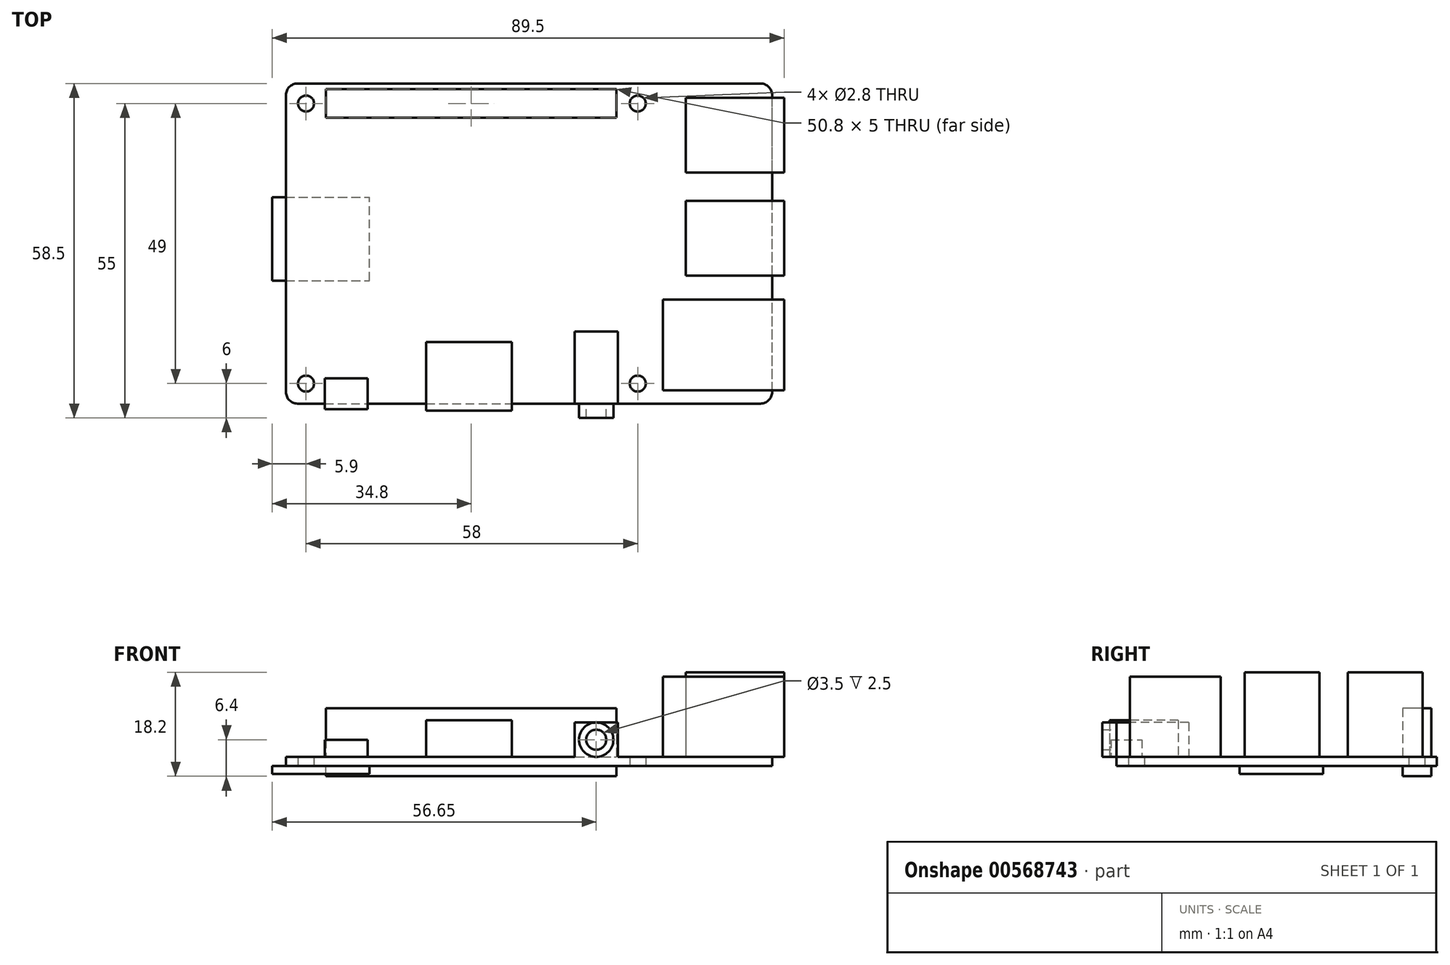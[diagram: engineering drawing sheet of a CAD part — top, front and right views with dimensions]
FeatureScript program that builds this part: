
annotation { "Feature Type Name" : "Feature", "Feature Type Description" : "" }
export const myFeature = defineFeature(function(context is Context, id is Id, definition is map)
    precondition{}
    {
        {
            var Q0;
            Q0=qCreatedBy(makeId("Top.planeOp"),FACE);
            var sketch = newSketch(context, id + "F0", { "sketchPlane" : qUnion([Q0])});
            skLineSegment(sketch, "E0.bottom", {"start": v(2, 0) * mm, "end": v(83, 0) * mm});
            skLineSegment(sketch, "E0.top", {"start": v(2, 56) * mm, "end": v(83, 56) * mm});
            skLineSegment(sketch, "E0.left", {"start": v(0, 2) * mm, "end": v(0, 54) * mm});
            skLineSegment(sketch, "E0.right", {"start": v(85, 2) * mm, "end": v(85, 54) * mm});
            skPoint(sketch, "E1.visualSharp", {"position": v(0, 56) * mm});
            skArc(sketch, "E1.filletArc", {"start": v(2, 56) * mm, "mid": v(0.59, 55.41) * mm, "end": v(0, 54) * mm});
            skPoint(sketch, "E2.visualSharp", {"position": v(85, 56) * mm});
            skArc(sketch, "E2.filletArc", {"start": v(85, 54) * mm, "mid": v(84.41, 55.41) * mm, "end": v(83, 56) * mm});
            skPoint(sketch, "E3.visualSharp", {"position": v(85, 0) * mm});
            skArc(sketch, "E3.filletArc", {"start": v(83, 0) * mm, "mid": v(84.41, 0.59) * mm, "end": v(85, 2) * mm});
            skPoint(sketch, "E4.visualSharp", {"position": v(0, 0) * mm});
            skArc(sketch, "E4.filletArc", {"start": v(0, 2) * mm, "mid": v(0.59, 0.59) * mm, "end": v(2, 0) * mm});
            skCircle(sketch, "E5", {"center": v(3.5, 52.5) * mm, "radius": 1.4 * mm});
            skCircle(sketch, "E6", {"center": v(61.5, 52.5) * mm, "radius": 1.4 * mm});
            skCircle(sketch, "E7", {"center": v(61.5, 3.5) * mm, "radius": 1.4 * mm});
            skCircle(sketch, "E8", {"center": v(3.5, 3.5) * mm, "radius": 1.4 * mm});
            skSolve(sketch);
        }
        {
            var Q0;
            Q0=makeQuery(id+"F0.imprint","IMPRINT",FACE,{"disambiguationData":[TD([[makeQuery(id+"F0.imprint","IMPRINT",EDGE,{"derivedFrom":sQuery(id+"F0.wireOp",EDGE,"E0.bottom")}),1.0]])]});
            extrude(context, id + "F1", {"entities" : qUnion([Q0]), "depth" : 1.6 * mm, "offsetDistance" : 25 * mm});
        }
        {
            var Q0;
            Q0=makeQuery(id+"F1.opExtrude","CAP_FACE",FACE,{"disambiguationData":[OSD([sQuery(id+"F0.wireOp",EDGE,"E0.bottom"),sQuery(id+"F0.wireOp",EDGE,"E0.top"),sQuery(id+"F0.wireOp",EDGE,"E0.left"),sQuery(id+"F0.wireOp",EDGE,"E0.right"),sQuery(id+"F0.wireOp",EDGE,"E1.filletArc"),sQuery(id+"F0.wireOp",EDGE,"E2.filletArc"),sQuery(id+"F0.wireOp",EDGE,"E3.filletArc"),sQuery(id+"F0.wireOp",EDGE,"E4.filletArc"),sQuery(id+"F0.wireOp",EDGE,"E5"),sQuery(id+"F0.wireOp",EDGE,"E6"),sQuery(id+"F0.wireOp",EDGE,"E7"),sQuery(id+"F0.wireOp",EDGE,"E8")])],"isStart":false});
            var sketch = newSketch(context, id + "F2", { "sketchPlane" : qUnion([Q0])});
            skLineSegment(sketch, "E9.bottom", {"start": v(87.1, 53.5) * mm, "end": v(69.9, 53.5) * mm});
            skLineSegment(sketch, "E9.top", {"start": v(87.1, 40.4) * mm, "end": v(69.9, 40.4) * mm});
            skLineSegment(sketch, "E9.left", {"start": v(87.1, 53.5) * mm, "end": v(87.1, 40.4) * mm});
            skLineSegment(sketch, "E9.right", {"start": v(69.9, 53.5) * mm, "end": v(69.9, 40.4) * mm});
            skLineSegment(sketch, "E10.bottom", {"start": v(87.1, 35.5) * mm, "end": v(69.9, 35.5) * mm});
            skLineSegment(sketch, "E10.top", {"start": v(87.1, 22.4) * mm, "end": v(69.9, 22.4) * mm});
            skLineSegment(sketch, "E10.left", {"start": v(87.1, 35.5) * mm, "end": v(87.1, 22.4) * mm});
            skLineSegment(sketch, "E10.right", {"start": v(69.9, 35.5) * mm, "end": v(69.9, 22.4) * mm});
            skLineSegment(sketch, "E11.bottom", {"start": v(87.1, 18.2) * mm, "end": v(65.9, 18.2) * mm});
            skLineSegment(sketch, "E11.top", {"start": v(87.1, 2.3) * mm, "end": v(65.9, 2.3) * mm});
            skLineSegment(sketch, "E11.left", {"start": v(87.1, 18.2) * mm, "end": v(87.1, 2.3) * mm});
            skLineSegment(sketch, "E11.right", {"start": v(65.9, 18.2) * mm, "end": v(65.9, 2.3) * mm});
            skSolve(sketch);
        }
        {
            var Q0;
            {var subQ0=sQuery(id+"F2.wireOp",EDGE,"E9.right");Q0=makeQuery(id+"F2.imprint","IMPRINT",FACE,{"disambiguationData":[TD([[makeQuery(id+"F2.imprint","IMPRINT",EDGE,{"derivedFrom":subQ0}),1.0]])]});}
            var Q1;
            {var subQ0=sQuery(id+"F2.wireOp",EDGE,"E9.left");Q1=makeQuery(id+"F2.imprint","IMPRINT",FACE,{"disambiguationData":[TD([[makeQuery(id+"F2.imprint","IMPRINT",EDGE,{"derivedFrom":subQ0}),-1.0]])]});}
            var Q2;
            {var subQ0=sQuery(id+"F2.wireOp",EDGE,"E10.right");Q2=makeQuery(id+"F2.imprint","IMPRINT",FACE,{"disambiguationData":[TD([[makeQuery(id+"F2.imprint","IMPRINT",EDGE,{"derivedFrom":subQ0}),1.0]])]});}
            var Q3;
            {var subQ0=sQuery(id+"F2.wireOp",EDGE,"E10.left");Q3=makeQuery(id+"F2.imprint","IMPRINT",FACE,{"disambiguationData":[TD([[makeQuery(id+"F2.imprint","IMPRINT",EDGE,{"derivedFrom":subQ0}),-1.0]])]});}
            extrude(context, id + "F3", {"entities" : qUnion([Q0, Q1, Q2, Q3]), "operationType" : NewBodyOperationType.ADD, "depth" : 14.8 * mm, "offsetDistance" : 25 * mm});
        }
        {
            var Q0;
            {var subQ0=sQuery(id+"F2.wireOp",EDGE,"E11.right");Q0=makeQuery(id+"F2.imprint","IMPRINT",FACE,{"disambiguationData":[TD([[makeQuery(id+"F2.imprint","IMPRINT",EDGE,{"derivedFrom":subQ0}),1.0]])]});}
            var Q1;
            {var subQ0=sQuery(id+"F2.wireOp",EDGE,"E11.left");Q1=makeQuery(id+"F2.imprint","IMPRINT",FACE,{"disambiguationData":[TD([[makeQuery(id+"F2.imprint","IMPRINT",EDGE,{"derivedFrom":subQ0}),-1.0]])]});}
            extrude(context, id + "F4", {"entities" : qUnion([Q0, Q1]), "operationType" : NewBodyOperationType.ADD, "depth" : 14 * mm, "offsetDistance" : 25 * mm});
        }
        {
            var Q0;
            Q0=makeQuery(id+"F1.opExtrude","CAP_FACE",FACE,{"disambiguationData":[OSD([sQuery(id+"F0.wireOp",EDGE,"E0.bottom"),sQuery(id+"F0.wireOp",EDGE,"E0.top"),sQuery(id+"F0.wireOp",EDGE,"E0.left"),sQuery(id+"F0.wireOp",EDGE,"E0.right"),sQuery(id+"F0.wireOp",EDGE,"E1.filletArc"),sQuery(id+"F0.wireOp",EDGE,"E2.filletArc"),sQuery(id+"F0.wireOp",EDGE,"E3.filletArc"),sQuery(id+"F0.wireOp",EDGE,"E4.filletArc"),sQuery(id+"F0.wireOp",EDGE,"E5"),sQuery(id+"F0.wireOp",EDGE,"E6"),sQuery(id+"F0.wireOp",EDGE,"E7"),sQuery(id+"F0.wireOp",EDGE,"E8")])],"isStart":false});
            var sketch = newSketch(context, id + "F5", { "sketchPlane" : qUnion([Q0])});
            skLineSegment(sketch, "E12.bottom", {"start": v(7, 55) * mm, "end": v(57.8, 55) * mm});
            skLineSegment(sketch, "E12.top", {"start": v(7, 50) * mm, "end": v(57.8, 50) * mm});
            skLineSegment(sketch, "E12.left", {"start": v(7, 55) * mm, "end": v(7, 50) * mm});
            skLineSegment(sketch, "E12.right", {"start": v(57.8, 55) * mm, "end": v(57.8, 50) * mm});
            skSolve(sketch);
        }
        {
            var Q0;
            Q0=makeQuery(id+"F5.imprint","IMPRINT",FACE,{"disambiguationData":[TD([[makeQuery(id+"F5.imprint","IMPRINT",EDGE,{"derivedFrom":sQuery(id+"F5.wireOp",EDGE,"E12.bottom")}),-1.0]])]});
            extrude(context, id + "F6", {"entities" : qUnion([Q0]), "operationType" : NewBodyOperationType.ADD, "depth" : 8.5 * mm, "offsetDistance" : 25 * mm});
        }
        {
            var Q0;
            Q0 = qSketchRegion(id + "F5", true);
            extrude(context, id + "F7", {"entities" : qUnion([Q0]), "operationType" : NewBodyOperationType.ADD, "oppositeDirection" : true, "depth" : (1.6 + 1.8) * mm, "offsetDistance" : 25 * mm});
        }
        {
            var Q0;
            Q0=makeQuery(id+"F1.opExtrude","CAP_FACE",FACE,{"disambiguationData":[OSD([sQuery(id+"F0.wireOp",EDGE,"E0.bottom"),sQuery(id+"F0.wireOp",EDGE,"E0.top"),sQuery(id+"F0.wireOp",EDGE,"E0.left"),sQuery(id+"F0.wireOp",EDGE,"E0.right"),sQuery(id+"F0.wireOp",EDGE,"E1.filletArc"),sQuery(id+"F0.wireOp",EDGE,"E2.filletArc"),sQuery(id+"F0.wireOp",EDGE,"E3.filletArc"),sQuery(id+"F0.wireOp",EDGE,"E4.filletArc"),sQuery(id+"F0.wireOp",EDGE,"E5"),sQuery(id+"F0.wireOp",EDGE,"E6"),sQuery(id+"F0.wireOp",EDGE,"E7"),sQuery(id+"F0.wireOp",EDGE,"E8")])],"isStart":true});
            var sketch = newSketch(context, id + "F8", { "sketchPlane" : qUnion([Q0])});
            skLineSegment(sketch, "E13.bottom", {"start": v(-2.4, -21.5) * mm, "end": v(14.6, -21.5) * mm});
            skLineSegment(sketch, "E13.top", {"start": v(-2.4, -36.1) * mm, "end": v(14.6, -36.1) * mm});
            skLineSegment(sketch, "E13.left", {"start": v(-2.4, -21.5) * mm, "end": v(-2.4, -36.1) * mm});
            skLineSegment(sketch, "E13.right", {"start": v(14.6, -21.5) * mm, "end": v(14.6, -36.1) * mm});
            skSolve(sketch);
        }
        {
            var Q0;
            Q0 = qSketchRegion(id + "F8", true);
            extrude(context, id + "F9", {"entities" : qUnion([Q0]), "operationType" : NewBodyOperationType.ADD, "depth" : 1.4 * mm, "offsetDistance" : 25 * mm});
        }
        {
            var Q0;
            Q0=makeQuery(id+"F1.opExtrude","CAP_FACE",FACE,{"disambiguationData":[OSD([sQuery(id+"F0.wireOp",EDGE,"E0.bottom"),sQuery(id+"F0.wireOp",EDGE,"E0.top"),sQuery(id+"F0.wireOp",EDGE,"E0.left"),sQuery(id+"F0.wireOp",EDGE,"E0.right"),sQuery(id+"F0.wireOp",EDGE,"E1.filletArc"),sQuery(id+"F0.wireOp",EDGE,"E2.filletArc"),sQuery(id+"F0.wireOp",EDGE,"E3.filletArc"),sQuery(id+"F0.wireOp",EDGE,"E4.filletArc"),sQuery(id+"F0.wireOp",EDGE,"E5"),sQuery(id+"F0.wireOp",EDGE,"E6"),sQuery(id+"F0.wireOp",EDGE,"E7"),sQuery(id+"F0.wireOp",EDGE,"E8")])],"isStart":false});
            var sketch = newSketch(context, id + "F10", { "sketchPlane" : qUnion([Q0])});
            skLineSegment(sketch, "E14.bottom", {"start": v(24.5, 10.8) * mm, "end": v(39.5, 10.8) * mm});
            skLineSegment(sketch, "E14.top", {"start": v(24.5, -1.2) * mm, "end": v(39.5, -1.2) * mm});
            skLineSegment(sketch, "E14.left", {"start": v(24.5, 10.8) * mm, "end": v(24.5, -1.2) * mm});
            skLineSegment(sketch, "E14.right", {"start": v(39.5, 10.8) * mm, "end": v(39.5, -1.2) * mm});
            skLineSegment(sketch, "E15.bottom", {"start": v(50.5, 12.6) * mm, "end": v(58, 12.6) * mm});
            skLineSegment(sketch, "E15.top", {"start": v(50.5, 0) * mm, "end": v(58, 0) * mm});
            skLineSegment(sketch, "E15.left", {"start": v(50.5, 12.6) * mm, "end": v(50.5, 0) * mm});
            skLineSegment(sketch, "E15.right", {"start": v(58, 12.6) * mm, "end": v(58, 0) * mm});
            skLineSegment(sketch, "E16.bottom", {"start": v(6.8, -1) * mm, "end": v(14.3, -1) * mm});
            skLineSegment(sketch, "E16.top", {"start": v(6.8, 4.4) * mm, "end": v(14.3, 4.4) * mm});
            skLineSegment(sketch, "E16.left", {"start": v(6.8, -1) * mm, "end": v(6.8, 4.4) * mm});
            skLineSegment(sketch, "E16.right", {"start": v(14.3, -1) * mm, "end": v(14.3, 4.4) * mm});
            skSolve(sketch);
        }
        {
            var Q0;
            {var subQ0=sQuery(id+"F10.wireOp",EDGE,"E16.top");Q0=makeQuery(id+"F10.imprint","IMPRINT",FACE,{"disambiguationData":[TD([[makeQuery(id+"F10.imprint","IMPRINT",EDGE,{"derivedFrom":subQ0}),-1.0]])]});}
            var Q1;
            {var subQ0=sQuery(id+"F10.wireOp",EDGE,"E16.bottom");Q1=makeQuery(id+"F10.imprint","IMPRINT",FACE,{"disambiguationData":[TD([[makeQuery(id+"F10.imprint","IMPRINT",EDGE,{"derivedFrom":subQ0}),1.0]])]});}
            extrude(context, id + "F11", {"entities" : qUnion([Q0, Q1]), "operationType" : NewBodyOperationType.ADD, "depth" : 3 * mm, "offsetDistance" : 25 * mm});
        }
        {
            var Q0;
            {var subQ0=sQuery(id+"F10.wireOp",EDGE,"E14.bottom");Q0=makeQuery(id+"F10.imprint","IMPRINT",FACE,{"disambiguationData":[TD([[makeQuery(id+"F10.imprint","IMPRINT",EDGE,{"derivedFrom":subQ0}),-1.0]])]});}
            var Q1;
            {var subQ0=sQuery(id+"F10.wireOp",EDGE,"E14.top");Q1=makeQuery(id+"F10.imprint","IMPRINT",FACE,{"disambiguationData":[TD([[makeQuery(id+"F10.imprint","IMPRINT",EDGE,{"derivedFrom":subQ0}),1.0]])]});}
            extrude(context, id + "F12", {"entities" : qUnion([Q0, Q1]), "operationType" : NewBodyOperationType.ADD, "depth" : 6.4 * mm, "offsetDistance" : 25 * mm});
        }
        {
            var Q0;
            Q0=makeQuery(id+"F10.imprint","IMPRINT",FACE,{"disambiguationData":[TD([[makeQuery(id+"F10.imprint","IMPRINT",EDGE,{"derivedFrom":sQuery(id+"F10.wireOp",EDGE,"E15.bottom")}),-1.0]])]});
            extrude(context, id + "F13", {"entities" : qUnion([Q0]), "operationType" : NewBodyOperationType.ADD, "depth" : 6 * mm, "offsetDistance" : 25 * mm});
        }
        {
            var Q0;
            Q0=makeQuery(id+"F13.boolean.opBoolean","MERGE",FACE,{"derivedFrom":[makeQuery(id+"F1.opExtrude","SWEPT_FACE",FACE,{"disambiguationData":[OSD([sQuery(id+"F0.wireOp",EDGE,"E0.bottom")])]}),makeQuery(id+"F13.opExtrude","SWEPT_FACE",FACE,{"disambiguationData":[OSD([sQuery(id+"F10.wireOp",EDGE,"E15.top")])]})]});
            var sketch = newSketch(context, id + "F14", { "sketchPlane" : qUnion([Q0])});
            skCircle(sketch, "E17", {"center": v(54.25, 4.6) * mm, "radius": 3 * mm});
            skCircle(sketch, "E18", {"center": v(54.25, 4.6) * mm, "radius": 1.75 * mm});
            skSolve(sketch);
        }
        {
            var Q0;
            Q0 = qSketchRegion(id + "F14", true);
            extrude(context, id + "F15", {"entities" : qUnion([Q0]), "operationType" : NewBodyOperationType.ADD, "depth" : 2.5 * mm, "offsetDistance" : 25 * mm});
        }
    });
